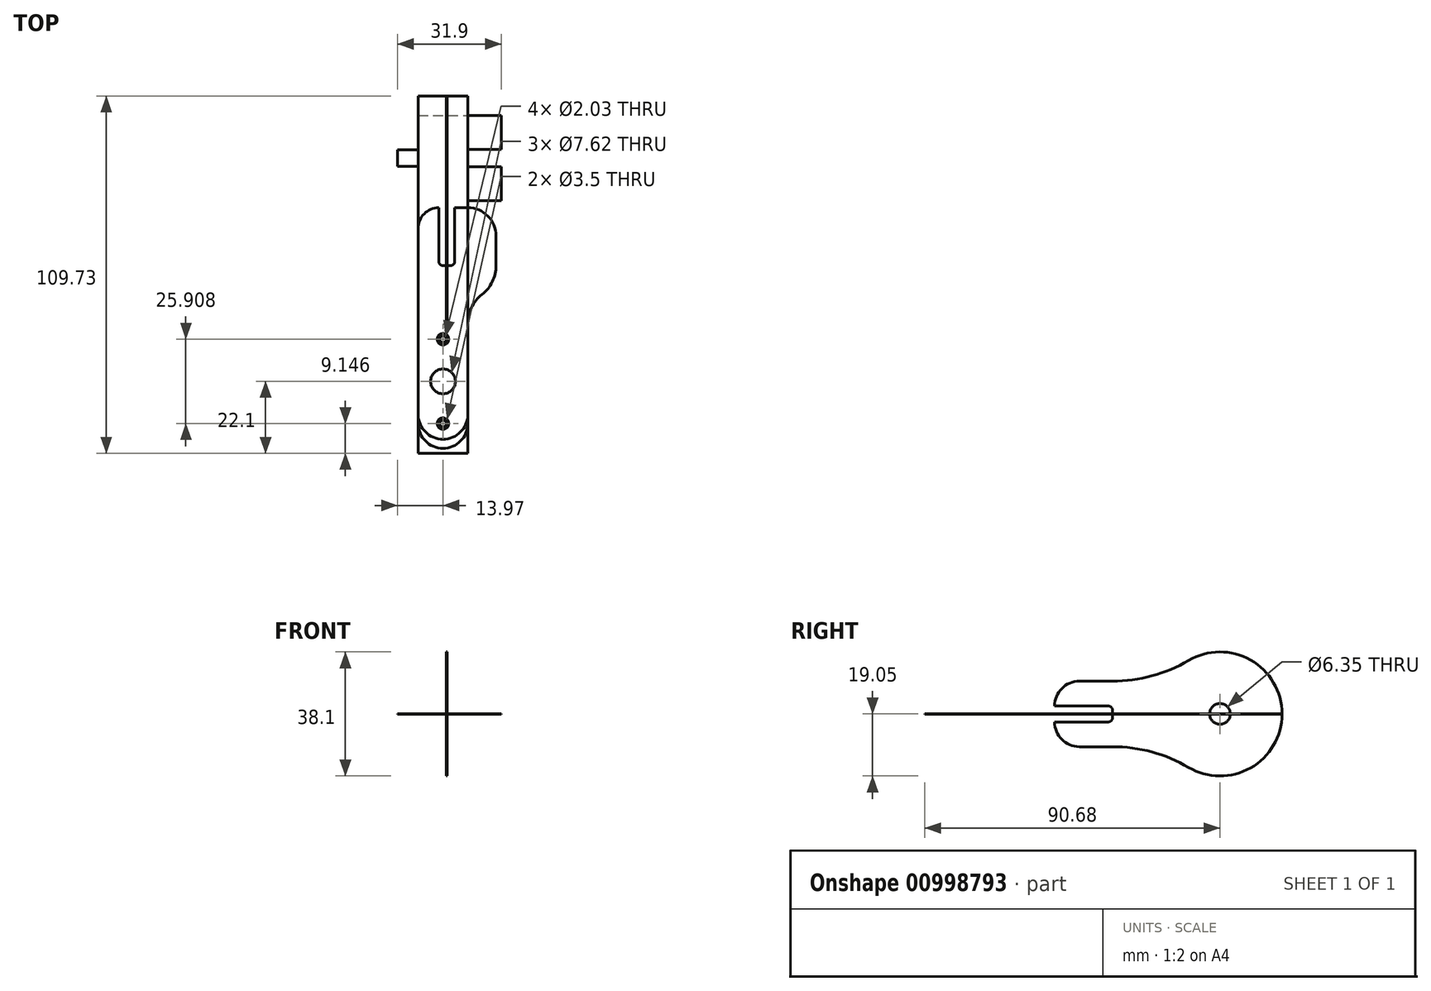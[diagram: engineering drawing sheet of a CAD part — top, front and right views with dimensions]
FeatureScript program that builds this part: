
annotation { "Feature Type Name" : "Feature", "Feature Type Description" : "" }
export const myFeature = defineFeature(function(context is Context, id is Id, definition is map)
    precondition{}
    {
        {
            assignVariable(context, id + "F0", {"name" : "absThickness", "anyValue" : .203});
        }
        {
            var Q0;
            Q0=qCreatedBy(makeId("Top.planeOp"),FACE);
            var sketch = newSketch(context, id + "F1", { "sketchPlane" : qUnion([Q0])});
            skLineSegment(sketch, "E0.bottom", {"start": v(-7.62, -22.1) * mm, "end": v(7.62, -22.1) * mm});
            skLineSegment(sketch, "E0.left", {"start": v(-7.62, -22.1) * mm, "end": v(-7.62, 81.61) * mm, "construction": true});
            skLineSegment(sketch, "E0.right", {"start": v(7.62, -22.1) * mm, "end": v(7.62, 81.61) * mm, "construction": true});
            skCircle(sketch, "E1", {"center": v(0, 0) * mm, "radius": 3.81 * mm});
            skLineSegment(sketch, "E2", {"start": v(0, 0) * mm, "end": v(0, -22.1) * mm, "construction": true});
            skLineSegment(sketch, "E3", {"start": v(-3.81, 0) * mm, "end": v(-7.62, 0) * mm, "construction": true});
            skLineSegment(sketch, "E4", {"start": v(0, -3.81) * mm, "end": v(0, -22.1) * mm, "construction": true});
            skCircle(sketch, "E5", {"center": v(0, -12.95) * mm, "radius": 1.02 * mm});
            skLineSegment(sketch, "E6", {"start": v(0, 0) * mm, "end": v(0, 12.95) * mm, "construction": true});
            skCircle(sketch, "E7", {"center": v(0, 12.95) * mm, "radius": 1.02 * mm});
            skLineSegment(sketch, "E8", {"start": v(0, 81.61) * mm, "end": v(0, 68.58) * mm, "construction": true});
            skLineSegment(sketch, "E9.bottom", {"start": v(-50.14, 17.78) * mm, "end": v(47.04, 17.78) * mm, "construction": true});
            skLineSegment(sketch, "E9.top", {"start": v(-50.14, -120.5) * mm, "end": v(47.04, -120.5) * mm, "construction": true});
            skLineSegment(sketch, "E9.left", {"start": v(-50.14, 17.78) * mm, "end": v(-50.14, -120.5) * mm, "construction": true});
            skLineSegment(sketch, "E9.right", {"start": v(47.04, 17.78) * mm, "end": v(47.04, -120.5) * mm, "construction": true});
            skLineSegment(sketch, "E10.bottom", {"start": v(7.62, 81.61) * mm, "end": v(17.93, 81.61) * mm});
            skLineSegment(sketch, "E10.top", {"start": v(7.62, 71.3) * mm, "end": v(17.93, 71.3) * mm});
            skLineSegment(sketch, "E10.right", {"start": v(17.93, 81.61) * mm, "end": v(17.93, 71.3) * mm});
            skLineSegment(sketch, "E11.bottom", {"start": v(7.62, 65.86) * mm, "end": v(17.93, 65.86) * mm});
            skLineSegment(sketch, "E11.top", {"start": v(7.62, 55.55) * mm, "end": v(17.93, 55.55) * mm});
            skLineSegment(sketch, "E11.right", {"start": v(17.93, 65.86) * mm, "end": v(17.93, 55.55) * mm});
            skLineSegment(sketch, "E12", {"start": v(17.93, 71.3) * mm, "end": v(17.93, 65.86) * mm, "construction": true});
            skLineSegment(sketch, "E13", {"start": v(17.93, 68.58) * mm, "end": v(0, 68.58) * mm, "construction": true});
            skLineSegment(sketch, "E14", {"start": v(7.62, 71.3) * mm, "end": v(7.62, 65.86) * mm});
            skLineSegment(sketch, "E15", {"start": v(7.62, 55.55) * mm, "end": v(7.62, -22.1) * mm});
            skLineSegment(sketch, "E16.bottom", {"start": v(-7.62, 66) * mm, "end": v(-13.97, 66) * mm});
            skLineSegment(sketch, "E16.top", {"start": v(-7.62, 71.16) * mm, "end": v(-13.97, 71.16) * mm});
            skLineSegment(sketch, "E16.right", {"start": v(-13.97, 66) * mm, "end": v(-13.97, 71.16) * mm});
            skLineSegment(sketch, "E17", {"start": v(-13.97, 68.58) * mm, "end": v(0, 68.58) * mm, "construction": true});
            skLineSegment(sketch, "E18", {"start": v(-7.62, 81.61) * mm, "end": v(7.62, 81.61) * mm});
            skLineSegment(sketch, "E19", {"start": v(-7.62, 66) * mm, "end": v(-7.62, -22.1) * mm});
            skLineSegment(sketch, "E20", {"start": v(-7.62, 81.61) * mm, "end": v(-7.62, 71.16) * mm});
            skSolve(sketch);
        }
        {
            var Q0;
            Q0 = qSketchRegion(id + "F1", true);
            extrude(context, id + "F2", {"entities" : qUnion([Q0]), "endBound" : BoundingType.SYMMETRIC, "depth" : (0.5 * getVariable(context, 'absThickness')) * mm, "offsetDistance" : 25.4 * mm});
        }
        {
            var Q0;
            Q0=qCreatedBy(makeId("Top.planeOp"),FACE);
            var sketch = newSketch(context, id + "F3", { "sketchPlane" : qUnion([Q0])});
            skCircle(sketch, "E21", {"center": v(0, 0) * mm, "radius": 3.81 * mm});
            skLineSegment(sketch, "E22", {"start": v(0, 0) * mm, "end": v(0, -20.57) * mm, "construction": true});
            skLineSegment(sketch, "E23", {"start": v(-3.8, 0) * mm, "end": v(-7.62, 0) * mm, "construction": true});
            skLineSegment(sketch, "E24", {"start": v(0, -3.81) * mm, "end": v(0, -20.57) * mm, "construction": true});
            skCircle(sketch, "E25", {"center": v(0, -12.95) * mm, "radius": 1.75 * mm});
            skLineSegment(sketch, "E26", {"start": v(0, 0) * mm, "end": v(0, 12.95) * mm, "construction": true});
            skCircle(sketch, "E27", {"center": v(0, 12.95) * mm, "radius": 1.75 * mm});
            skLineSegment(sketch, "E28.bottom", {"start": v(-50.14, 17.78) * mm, "end": v(50.14, 17.78) * mm, "construction": true});
            skLineSegment(sketch, "E28.top", {"start": v(-50.14, -120.5) * mm, "end": v(50.14, -120.5) * mm, "construction": true});
            skLineSegment(sketch, "E28.left", {"start": v(-50.14, 17.78) * mm, "end": v(-50.14, -120.5) * mm, "construction": true});
            skLineSegment(sketch, "E28.right", {"start": v(50.14, 17.78) * mm, "end": v(50.14, -120.5) * mm, "construction": true});
            skLineSegment(sketch, "E29", {"start": v(7.62, 26.67) * mm, "end": v(7.62, -12.95) * mm});
            skLineSegment(sketch, "E30", {"start": v(-7.62, 53.34) * mm, "end": v(-7.62, -12.95) * mm});
            skLineSegment(sketch, "E31", {"start": v(7.62, 26.67) * mm, "end": v(16.3, 26.67) * mm, "construction": true});
            skLineSegment(sketch, "E32", {"start": v(16.3, 26.67) * mm, "end": v(16.3, 44.65) * mm});
            skLineSegment(sketch, "E33", {"start": v(7.62, 53.34) * mm, "end": v(3.6, 53.34) * mm});
            skLineSegment(sketch, "E34", {"start": v(3.6, 53.34) * mm, "end": v(3.6, 35.56) * mm});
            skLineSegment(sketch, "E35", {"start": v(3.6, 35.56) * mm, "end": v(-1.27, 35.56) * mm});
            skLineSegment(sketch, "E36", {"start": v(-1.27, 35.56) * mm, "end": v(-1.27, 53.34) * mm});
            skLineSegment(sketch, "E37", {"start": v(-1.27, 53.34) * mm, "end": v(-7.62, 53.34) * mm});
            skLineSegment(sketch, "E38", {"start": v(0, 17.78) * mm, "end": v(0, 68.58) * mm, "construction": true});
            skLineSegment(sketch, "E39", {"start": v(0, 68.58) * mm, "end": v(-50.14, 68.58) * mm, "construction": true});
            skLineSegment(sketch, "E40", {"start": v(1.17, 35.56) * mm, "end": v(1.17, 17.78) * mm, "construction": true});
            skLineSegment(sketch, "E41", {"start": v(1.17, 26.67) * mm, "end": v(7.62, 26.67) * mm, "construction": true});
            skArc(sketch, "E42", {"start": v(11.96, 26.67) * mm, "mid": v(8.76, 22.73) * mm, "end": v(7.62, 17.78) * mm});
            skArc(sketch, "E43", {"start": v(11.96, 26.67) * mm, "mid": v(15.16, 30.61) * mm, "end": v(16.3, 35.56) * mm});
            skPoint(sketch, "E44", {"position": v(16.3, 40) * mm});
            skPoint(sketch, "E45.visualSharp", {"position": v(16.3, 53.34) * mm});
            skArc(sketch, "E45.filletArc", {"start": v(16.3, 44.65) * mm, "mid": v(13.76, 50.8) * mm, "end": v(7.62, 53.34) * mm});
            skArc(sketch, "E46", {"start": v(-7.62, -12.95) * mm, "mid": v(0, -20.57) * mm, "end": v(7.62, -12.95) * mm});
            skSolve(sketch);
        }
        {
            var Q0;
            Q0 = qSketchRegion(id + "F3", true);
            extrude(context, id + "F4", {"entities" : qUnion([Q0]), "endBound" : BoundingType.SYMMETRIC, "depth" : (getVariable(context, 'absThickness')) * mm, "offsetDistance" : 25.4 * mm});
        }
        {
            var Q0;
            Q0=makeQuery(id+"F4.opExtrude","SWEPT_EDGE",EDGE,{"disambiguationData":[OSD([sQuery(id+"F3.wireOp",EDGE,"E34"),sQuery(id+"F3.wireOp",EDGE,"E35")])]});
            var Q1;
            Q1=makeQuery(id+"F4.opExtrude","SWEPT_EDGE",EDGE,{"disambiguationData":[OSD([sQuery(id+"F3.wireOp",EDGE,"E35"),sQuery(id+"F3.wireOp",EDGE,"E36")])]});
            fillet(context, id + "F5", {"entities" : qUnion([Q0, Q1]), "radius" : 1.27 * mm, "tangentPropagation" : true, "allowEdgeOverflow" : false});
        }
        {
            var Q0;
            Q0=makeQuery(id+"F4.opExtrude","SWEPT_EDGE",EDGE,{"disambiguationData":[OSD([sQuery(id+"F3.wireOp",EDGE,"E30"),sQuery(id+"F3.wireOp",EDGE,"E37")])]});
            fillet(context, id + "F6", {"entities" : qUnion([Q0]), "radius" : 6.35 * mm, "tangentPropagation" : true, "allowEdgeOverflow" : false});
        }
        {
            var Q0;
            Q0=sQuery(id+"F3.wireOp",EDGE,"E35");
            cPoint(context, id + "F7", {"entities" : qUnion([Q0]), "parameter" : 0.5});
        }
        {
            var Q0;
            Q0 = qCreatedBy(id + "F7" ,VERTEX);
            var Q1;
            Q1=qCreatedBy(makeId("Right.planeOp"),FACE);
            cPlane(context, id + "F8", {"entities" : qUnion([Q0, Q1]), "cplaneType" : CPlaneType.PLANE_POINT, "offset" : 25.4 * mm, "width" : 152.4 * mm, "height" : 152.4 * mm});
        }
        {
            var Q0;
            Q0=qCreatedBy(id+"F8.planeOp",FACE);
            var sketch = newSketch(context, id + "F9", { "sketchPlane" : qUnion([Q0])});
            skCircle(sketch, "E47", {"center": v(68.58, 0) * mm, "radius": 3.18 * mm});
            skCircle(sketch, "E48", {"center": v(68.58, 0) * mm, "radius": 19.05 * mm});
            skArc(sketch, "E49", {"start": v(58.92, -16.42) * mm, "mid": v(47.67, -11.68) * mm, "end": v(35.56, -10.06) * mm});
            skLineSegment(sketch, "E50", {"start": v(35.56, -10.06) * mm, "end": v(35.56, 0) * mm, "construction": true});
            skLineSegment(sketch, "E51", {"start": v(68.58, 0) * mm, "end": v(35.56, 0) * mm, "construction": true});
            skLineSegment(sketch, "E52", {"start": v(35.56, -10.06) * mm, "end": v(17.78, -10.06) * mm});
            skLineSegment(sketch, "E53", {"start": v(17.78, -10.06) * mm, "end": v(17.78, -2.44) * mm});
            skLineSegment(sketch, "E54", {"start": v(17.78, -2.44) * mm, "end": v(35.56, -2.44) * mm});
            skLineSegment(sketch, "E55", {"start": v(35.56, -2.44) * mm, "end": v(35.56, 0) * mm});
            skLineSegment(sketch, "E56.MirrorCS", {"start": v(35.56, 2.44) * mm, "end": v(35.56, 0) * mm});
            skLineSegment(sketch, "E57.MirrorCS", {"start": v(17.78, 2.44) * mm, "end": v(35.56, 2.44) * mm});
            skLineSegment(sketch, "E58.MirrorCS", {"start": v(17.78, 10.06) * mm, "end": v(17.78, 2.44) * mm});
            skLineSegment(sketch, "E59.MirrorCS", {"start": v(35.56, 10.06) * mm, "end": v(17.78, 10.06) * mm});
            skArc(sketch, "E60.MirrorCS", {"start": v(58.92, 16.42) * mm, "mid": v(47.67, 11.68) * mm, "end": v(35.56, 10.06) * mm});
            skSolve(sketch);
        }
        {
            var Q0;
            Q0 = qSketchRegion(id + "F9", true);
            extrude(context, id + "F10", {"entities" : qUnion([Q0]), "endBound" : BoundingType.SYMMETRIC, "depth" : (getVariable(context, 'absThickness')) * mm, "offsetDistance" : 25.4 * mm});
        }
        {
            var Q0;
            Q0=makeQuery(id+"F10.opExtrude","SWEPT_EDGE",EDGE,{"disambiguationData":[OSD([sQuery(id+"F9.wireOp",EDGE,"E56.MirrorCS"),sQuery(id+"F9.wireOp",EDGE,"E57.MirrorCS")])]});
            var Q1;
            Q1=makeQuery(id+"F10.opExtrude","SWEPT_EDGE",EDGE,{"disambiguationData":[OSD([sQuery(id+"F9.wireOp",EDGE,"E54"),sQuery(id+"F9.wireOp",EDGE,"E55")])]});
            fillet(context, id + "F11", {"entities" : qUnion([Q0, Q1]), "radius" : 1.27 * mm, "tangentPropagation" : true, "allowEdgeOverflow" : false});
        }
        {
            var Q0;
            Q0=makeQuery(id+"F10.opExtrude","SWEPT_EDGE",EDGE,{"disambiguationData":[OSD([sQuery(id+"F9.wireOp",EDGE,"E52"),sQuery(id+"F9.wireOp",EDGE,"E53")])]});
            var Q1;
            Q1=makeQuery(id+"F10.opExtrude","SWEPT_EDGE",EDGE,{"disambiguationData":[OSD([sQuery(id+"F9.wireOp",EDGE,"E58.MirrorCS"),sQuery(id+"F9.wireOp",EDGE,"E59.MirrorCS")])]});
            fillet(context, id + "F12", {"entities" : qUnion([Q0, Q1]), "radius" : 7.62 * mm, "tangentPropagation" : true, "allowEdgeOverflow" : false});
        }
        {
            var Q0;
            Q0=qCreatedBy(makeId("Top.planeOp"),FACE);
            var sketch = newSketch(context, id + "F13", { "sketchPlane" : qUnion([Q0])});
            skLineSegment(sketch, "E61.bottom", {"start": v(-7.62, -17.78) * mm, "end": v(7.62, -17.78) * mm});
            skLineSegment(sketch, "E61.left", {"start": v(-7.62, -17.78) * mm, "end": v(-7.62, 87.63) * mm});
            skCircle(sketch, "E62", {"center": v(0, 0) * mm, "radius": 3.81 * mm});
            skLineSegment(sketch, "E63", {"start": v(0, 0) * mm, "end": v(0, -17.78) * mm, "construction": true});
            skLineSegment(sketch, "E64", {"start": v(-3.8, 0) * mm, "end": v(-7.62, 0) * mm, "construction": true});
            skCircle(sketch, "E65", {"center": v(0, -12.95) * mm, "radius": 1.02 * mm});
            skLineSegment(sketch, "E66", {"start": v(0, 0) * mm, "end": v(0, 12.95) * mm, "construction": true});
            skCircle(sketch, "E67", {"center": v(0, 12.95) * mm, "radius": 1.02 * mm});
            skLineSegment(sketch, "E68", {"start": v(0, 87.63) * mm, "end": v(0, 68.58) * mm, "construction": true});
            skLineSegment(sketch, "E69.bottom", {"start": v(-52.4, 17.78) * mm, "end": v(44.77, 17.78) * mm, "construction": true});
            skLineSegment(sketch, "E69.top", {"start": v(-52.4, -154.6) * mm, "end": v(44.77, -154.6) * mm, "construction": true});
            skLineSegment(sketch, "E69.left", {"start": v(-52.4, 17.78) * mm, "end": v(-52.4, -154.6) * mm, "construction": true});
            skLineSegment(sketch, "E69.right", {"start": v(44.77, 17.78) * mm, "end": v(44.77, -154.6) * mm, "construction": true});
            skLineSegment(sketch, "E70", {"start": v(7.62, 68.58) * mm, "end": v(0, 68.58) * mm, "construction": true});
            skLineSegment(sketch, "E71", {"start": v(-7.62, 68.58) * mm, "end": v(0, 68.58) * mm, "construction": true});
            skLineSegment(sketch, "E72", {"start": v(-7.62, 87.63) * mm, "end": v(7.62, 87.63) * mm});
            skLineSegment(sketch, "E73", {"start": v(7.62, 87.63) * mm, "end": v(7.62, -17.78) * mm});
            skLineSegment(sketch, "E74", {"start": v(0, 0) * mm, "end": v(0, 17.78) * mm, "construction": true});
            skSolve(sketch);
        }
        {
            var Q0;
            Q0 = qSketchRegion(id + "F13", true);
            extrude(context, id + "F14", {"entities" : qUnion([Q0]), "endBound" : BoundingType.SYMMETRIC, "depth" : (getVariable(context, 'absThickness')) * mm, "offsetDistance" : 25.4 * mm});
        }
        {
            var Q0;
            Q0=makeQuery(id+"F14.opExtrude","SWEPT_EDGE",EDGE,{"disambiguationData":[OSD([sQuery(id+"F13.wireOp",EDGE,"E61.bottom"),sQuery(id+"F13.wireOp",EDGE,"E73")])]});
            var Q1;
            Q1=makeQuery(id+"F14.opExtrude","SWEPT_EDGE",EDGE,{"disambiguationData":[OSD([sQuery(id+"F13.wireOp",EDGE,"E61.bottom"),sQuery(id+"F13.wireOp",EDGE,"E61.left")])]});
            fillet(context, id + "F15", {"entities" : qUnion([Q0, Q1]), "radius" : 7.62 * mm, "tangentPropagation" : true, "allowEdgeOverflow" : false});
        }
    });
